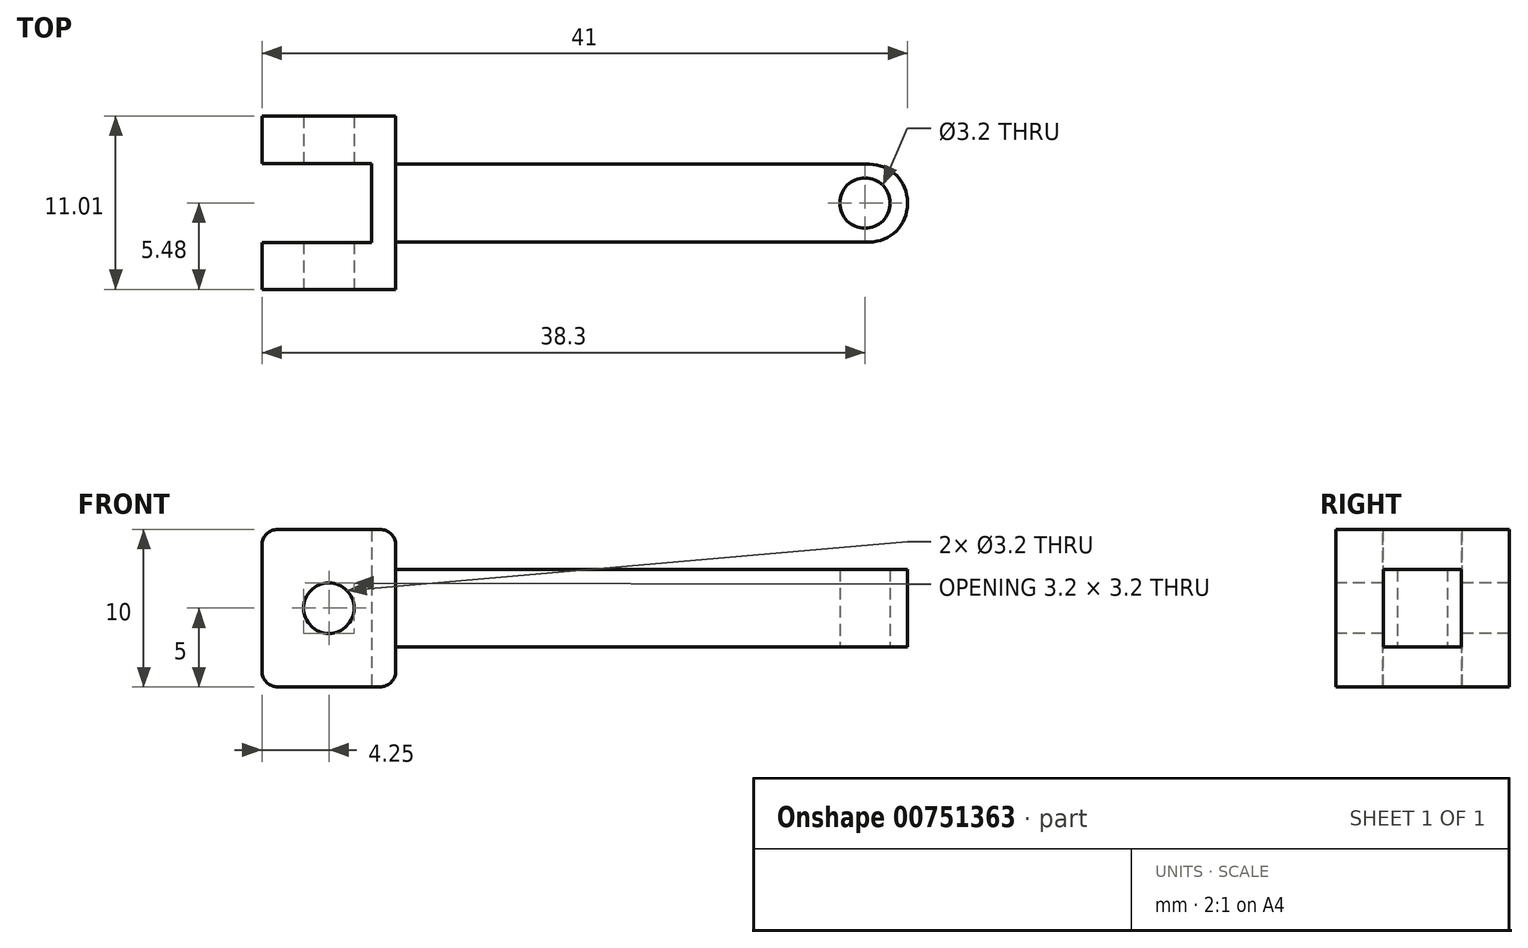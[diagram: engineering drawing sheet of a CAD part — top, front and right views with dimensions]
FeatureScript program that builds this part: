
annotation { "Feature Type Name" : "Feature", "Feature Type Description" : "" }
export const myFeature = defineFeature(function(context is Context, id is Id, definition is map)
    precondition{}
    {
        {
            var Q0;
            Q0=qCreatedBy(makeId("Top.planeOp"),FACE);
            var sketch = newSketch(context, id + "F0", { "sketchPlane" : qUnion([Q0])});
            skLineSegment(sketch, "E0.bottom", {"start": v(13.83, -2.48) * mm, "end": v(-13.83, -2.48) * mm});
            skLineSegment(sketch, "E0.top", {"start": v(13.83, 2.48) * mm, "end": v(-13.83, 2.47) * mm});
            skLineSegment(sketch, "E0.left", {"start": v(16.25, -0.05) * mm, "end": v(16.25, 0.05) * mm});
            skLineSegment(sketch, "E0.right", {"start": v(-16.25, -0.05) * mm, "end": v(-16.25, -0.05) * mm});
            skPoint(sketch, "E0.middle", {"position": v(0, 0) * mm});
            skPoint(sketch, "E1", {"position": v(-16.25, 0) * mm});
            skPoint(sketch, "E2", {"position": v(16.25, 0) * mm});
            skPoint(sketch, "E3.visualSharp", {"position": v(16.25, 2.48) * mm});
            skArc(sketch, "E3.filletArc", {"start": v(16.25, 0.05) * mm, "mid": v(15.54, 1.76) * mm, "end": v(13.83, 2.48) * mm});
            skPoint(sketch, "E4.visualSharp", {"position": v(16.25, -2.47) * mm});
            skArc(sketch, "E4.filletArc", {"start": v(13.83, -2.48) * mm, "mid": v(15.54, -1.76) * mm, "end": v(16.25, -0.05) * mm});
            skPoint(sketch, "E5", {"position": v(13.55, 0) * mm});
            skCircle(sketch, "E6", {"center": v(13.55, 0) * mm, "radius": 1.6 * mm});
            skPoint(sketch, "E7.visualSharp", {"position": v(-16.25, 2.47) * mm});
            skPoint(sketch, "E8.visualSharp", {"position": v(-16.25, -2.48) * mm});
            skPoint(sketch, "E9", {"position": v(8.75, 0) * mm});
            skPoint(sketch, "E10", {"position": v(8.75, -2.48) * mm});
            skLineSegment(sketch, "E11.bottom", {"start": v(-6.33, 2.48) * mm, "end": v(13.83, 2.48) * mm});
            skLineSegment(sketch, "E11.top", {"start": v(-6.33, -2.48) * mm, "end": v(13.83, -2.48) * mm});
            skLineSegment(sketch, "E11.right", {"start": v(8.75, -0.05) * mm, "end": v(8.75, -0.05) * mm});
            skPoint(sketch, "E12.visualSharp", {"position": v(8.75, 2.48) * mm});
            skLineSegment(sketch, "E13.bottom", {"start": v(-16.25, 2.47) * mm, "end": v(-13.83, 2.47) * mm});
            skLineSegment(sketch, "E13.top", {"start": v(-16.25, -2.48) * mm, "end": v(-13.83, -2.48) * mm});
            skLineSegment(sketch, "E13.left", {"start": v(-16.25, 2.47) * mm, "end": v(-16.25, -2.48) * mm});
            skLineSegment(sketch, "E14.top", {"start": v(-16.25, 2.48) * mm, "end": v(-8.75, 2.48) * mm});
            skLineSegment(sketch, "E14.left", {"start": v(-16.25, -2.48) * mm, "end": v(-16.25, 2.47) * mm});
            skPoint(sketch, "E15", {"position": v(0, 2.48) * mm});
            skPoint(sketch, "E16", {"position": v(3.75, -2.48) * mm});
            skSolve(sketch);
        }
        {
            var Q0;
            {var subQ4=sQuery(id+"F0.wireOp",EDGE,"E3.filletArc");Q0=makeQuery(id+"F0.imprint","IMPRINT",FACE,{"disambiguationData":[TD([[makeQuery(id+"F0.imprint","IMPRINT",EDGE,{"derivedFrom":subQ4}),1.0]])]});}
            extrude(context, id + "F1", {"entities" : qUnion([Q0]), "depth" : 2.45 * mm, "offsetDistance" : 25 * mm});
        }
        {
            var Q0;
            Q0=makeQuery(id+"F1.opExtrude","SWEPT_BODY",BODY,{"disambiguationData":[OSD([sQuery(id+"F0.wireOp",EDGE,"E0.bottom"),sQuery(id+"F0.wireOp",EDGE,"E0.top"),sQuery(id+"F0.wireOp",EDGE,"E3.filletArc"),sQuery(id+"F0.wireOp",EDGE,"E4.filletArc"),sQuery(id+"F0.wireOp",EDGE,"E6"),sQuery(id+"F0.wireOp",EDGE,"E11.bottom"),sQuery(id+"F0.wireOp",EDGE,"E11.top"),sQuery(id+"F0.wireOp",EDGE,"E14.right")])]});
            var Q1;
            Q1=qCreatedBy(makeId("Top.planeOp"),FACE);
            mirror(context, id + "F2", {"operationType" : NewBodyOperationType.ADD, "entities" : qUnion([Q0]), "mirrorPlane" : qUnion([Q1])});
        }
        {
            var Q0;
            {var subQ0=makeQuery(id+"F1.opExtrude","SWEPT_FACE",FACE,{"disambiguationData":[OSD([sQuery(id+"F0.wireOp",EDGE,"E0.bottom"),sQuery(id+"F0.wireOp",EDGE,"E11.top"),sQuery(id+"F0.wireOp",EDGE,"E13.top")])]});Q0=makeQuery(id+"F2.boolean.opBoolean","MERGE",FACE,{"derivedFrom":[subQ0,makeQuery(id+"F2.opPattern","COPY",FACE,{"derivedFrom":subQ0,"instanceName":"1"})]});}
            var sketch = newSketch(context, id + "F3", { "sketchPlane" : qUnion([Q0])});
            skLineSegment(sketch, "E17.top", {"start": v(-16.25, 0) * mm, "end": v(-24.75, 0) * mm});
            skLineSegment(sketch, "E17.left", {"start": v(-16.25, -2.45) * mm, "end": v(-16.25, 0) * mm});
            skLineSegment(sketch, "E17.right", {"start": v(-24.75, 0) * mm, "end": v(-24.75, 0) * mm});
            skLineSegment(sketch, "E18.MirrorCS", {"start": v(-16.25, 2.45) * mm, "end": v(-16.25, 0) * mm});
            skLineSegment(sketch, "E19.top", {"start": v(-17.25, 5) * mm, "end": v(-23.75, 5) * mm});
            skLineSegment(sketch, "E19.left", {"start": v(-16.25, 0) * mm, "end": v(-16.25, 4) * mm});
            skLineSegment(sketch, "E19.right", {"start": v(-24.75, 0) * mm, "end": v(-24.75, 4) * mm});
            skPoint(sketch, "E20.visualSharp", {"position": v(-16.25, 5) * mm});
            skArc(sketch, "E20.filletArc", {"start": v(-16.25, 4) * mm, "mid": v(-16.54, 4.7) * mm, "end": v(-17.25, 5) * mm});
            skPoint(sketch, "E21.visualSharp", {"position": v(-24.75, 5) * mm});
            skArc(sketch, "E21.filletArc", {"start": v(-23.75, 5) * mm, "mid": v(-24.46, 4.7) * mm, "end": v(-24.75, 4) * mm});
            skSolve(sketch);
        }
        {
            var Q0;
            Q0 = qSketchRegion(id + "F3", true);
            extrude(context, id + "F4", {"entities" : qUnion([Q0]), "operationType" : NewBodyOperationType.ADD, "oppositeDirection" : true, "depth" : 8 * mm, "offsetDistance" : 25 * mm});
        }
        {
            var Q0;
            Q0=makeQuery(id+"F1.opExtrude","SWEPT_BODY",BODY,{"disambiguationData":[OSD([sQuery(id+"F0.wireOp",EDGE,"E0.bottom"),sQuery(id+"F0.wireOp",EDGE,"E0.top"),sQuery(id+"F0.wireOp",EDGE,"E0.left"),sQuery(id+"F0.wireOp",EDGE,"E3.filletArc"),sQuery(id+"F0.wireOp",EDGE,"E4.filletArc"),sQuery(id+"F0.wireOp",EDGE,"E6"),sQuery(id+"F0.wireOp",EDGE,"E11.bottom"),sQuery(id+"F0.wireOp",EDGE,"E11.top"),sQuery(id+"F0.wireOp",EDGE,"E13.top"),sQuery(id+"F0.wireOp",EDGE,"E14.top"),sQuery(id+"F0.wireOp",EDGE,"E14.left")])]});
            var Q1;
            Q1=qCreatedBy(makeId("Top.planeOp"),FACE);
            mirror(context, id + "F5", {"operationType" : NewBodyOperationType.ADD, "entities" : qUnion([Q0]), "mirrorPlane" : qUnion([Q1])});
        }
        {
            var Q0;
            {var subQ0=makeQuery(id+"F1.opExtrude","SWEPT_FACE",FACE,{"disambiguationData":[OSD([sQuery(id+"F0.wireOp",EDGE,"E0.bottom"),sQuery(id+"F0.wireOp",EDGE,"E11.top"),sQuery(id+"F0.wireOp",EDGE,"E13.top")])]});var subQ1=makeQuery(id+"F4.boolean.opBoolean","MERGE",FACE,{"derivedFrom":[makeQuery(id+"F2.boolean.opBoolean","MERGE",FACE,{"derivedFrom":[subQ0,makeQuery(id+"F2.opPattern","COPY",FACE,{"derivedFrom":subQ0,"instanceName":"1"})]}),makeQuery(id+"F4.opExtrude","CAP_FACE",FACE,{"disambiguationData":[OSD([sQuery(id+"F3.wireOp",EDGE,"E17.top"),sQuery(id+"F3.wireOp",EDGE,"E19.top"),sQuery(id+"F3.wireOp",EDGE,"E19.left"),sQuery(id+"F3.wireOp",EDGE,"E19.right"),sQuery(id+"F3.wireOp",EDGE,"E20.filletArc"),sQuery(id+"F3.wireOp",EDGE,"E21.filletArc")])],"isStart":true})]});Q0=makeQuery(id+"F5.boolean.opBoolean","MERGE",FACE,{"derivedFrom":[subQ1,makeQuery(id+"F5.opPattern","COPY",FACE,{"derivedFrom":subQ1,"instanceName":"1"})]});}
            var sketch = newSketch(context, id + "F6", { "sketchPlane" : qUnion([Q0])});
            skLineSegment(sketch, "E22", {"start": v(-20.5, 0) * mm, "end": v(-20.5, 5) * mm, "construction": true});
            skPoint(sketch, "E22.startSnap0", {"position": v(-20.5, 5) * mm});
            skCircle(sketch, "E23", {"center": v(-20.5, 0) * mm, "radius": 1.6 * mm});
            skSolve(sketch);
        }
        {
            var Q0;
            Q0=makeQuery(id+"F6.imprint","IMPRINT",FACE,{"disambiguationData":[TD([[makeQuery(id+"F6.imprint","IMPRINT",EDGE,{"derivedFrom":sQuery(id+"F6.wireOp",EDGE,"E23")}),1.0]])]});
            extrude(context, id + "F7", {"entities" : qUnion([Q0]), "operationType" : NewBodyOperationType.REMOVE, "oppositeDirection" : true, "depth" : 25 * mm, "offsetDistance" : 25 * mm});
        }
        {
            var Q0;
            {var subQ0=makeQuery(id+"F4.opExtrude","CAP_FACE",FACE,{"disambiguationData":[OSD([sQuery(id+"F3.wireOp",EDGE,"E17.top"),sQuery(id+"F3.wireOp",EDGE,"E19.top"),sQuery(id+"F3.wireOp",EDGE,"E19.left"),sQuery(id+"F3.wireOp",EDGE,"E19.right"),sQuery(id+"F3.wireOp",EDGE,"E20.filletArc"),sQuery(id+"F3.wireOp",EDGE,"E21.filletArc")])],"isStart":false});Q0=makeQuery(id+"F5.boolean.opBoolean","MERGE",FACE,{"derivedFrom":[subQ0,makeQuery(id+"F5.opPattern","COPY",FACE,{"derivedFrom":subQ0,"instanceName":"1"})]});}
            extrude(context, id + "F8", {"entities" : qUnion([Q0]), "operationType" : NewBodyOperationType.ADD, "oppositeDirection" : true, "depth" : 11 * mm, "offsetDistance" : 25 * mm});
        }
        {
            var Q0;
            {var subQ0=sQuery(id+"F3.wireOp",EDGE,"E19.top");Q0=makeQuery(id+"F8.boolean.opBoolean","MERGE",FACE,{"derivedFrom":[makeQuery(id+"F5.opPattern","COPY",FACE,{"derivedFrom":makeQuery(id+"F4.opExtrude","SWEPT_FACE",FACE,{"disambiguationData":[OSD([subQ0])]}),"instanceName":"1"}),makeQuery(id+"F8.opExtrude","SWEPT_FACE",FACE,{"disambiguationData":[OSD([subQ0]),TDD([makeQuery(id+"F5.opPattern","COPY",EDGE,{"derivedFrom":makeQuery(id+"F4.opExtrude","CAP_EDGE",EDGE,{"disambiguationData":[OSD([subQ0])],"isStart":false}),"instanceName":"1"})])]})]});}
            var sketch = newSketch(context, id + "F9", { "sketchPlane" : qUnion([Q0])});
            skLineSegment(sketch, "E24", {"start": v(-25.3, 0) * mm, "end": v(0, 0) * mm, "construction": true});
            skPoint(sketch, "E25", {"position": v(-20.5, -0.02) * mm});
            skLineSegment(sketch, "E26.bottom", {"start": v(-25.3, 0) * mm, "end": v(-17.8, 0) * mm});
            skLineSegment(sketch, "E26.top", {"start": v(-25.3, 2.5) * mm, "end": v(-17.8, 2.5) * mm});
            skLineSegment(sketch, "E26.left", {"start": v(-25.3, 0) * mm, "end": v(-25.3, 2.5) * mm});
            skLineSegment(sketch, "E26.right", {"start": v(-17.8, 0) * mm, "end": v(-17.8, 2.5) * mm});
            skLineSegment(sketch, "E27.top", {"start": v(-25.3, -2.5) * mm, "end": v(-17.8, -2.5) * mm});
            skLineSegment(sketch, "E27.left", {"start": v(-25.3, 0) * mm, "end": v(-25.3, -2.5) * mm});
            skLineSegment(sketch, "E27.right", {"start": v(-17.8, 0) * mm, "end": v(-17.8, -2.5) * mm});
            skSolve(sketch);
        }
        {
            var Q0;
            Q0 = qSketchRegion(id + "F9", true);
            extrude(context, id + "F10", {"entities" : qUnion([Q0]), "operationType" : NewBodyOperationType.REMOVE, "oppositeDirection" : true, "depth" : 14.3 * mm, "offsetDistance" : 25 * mm});
        }
    });
